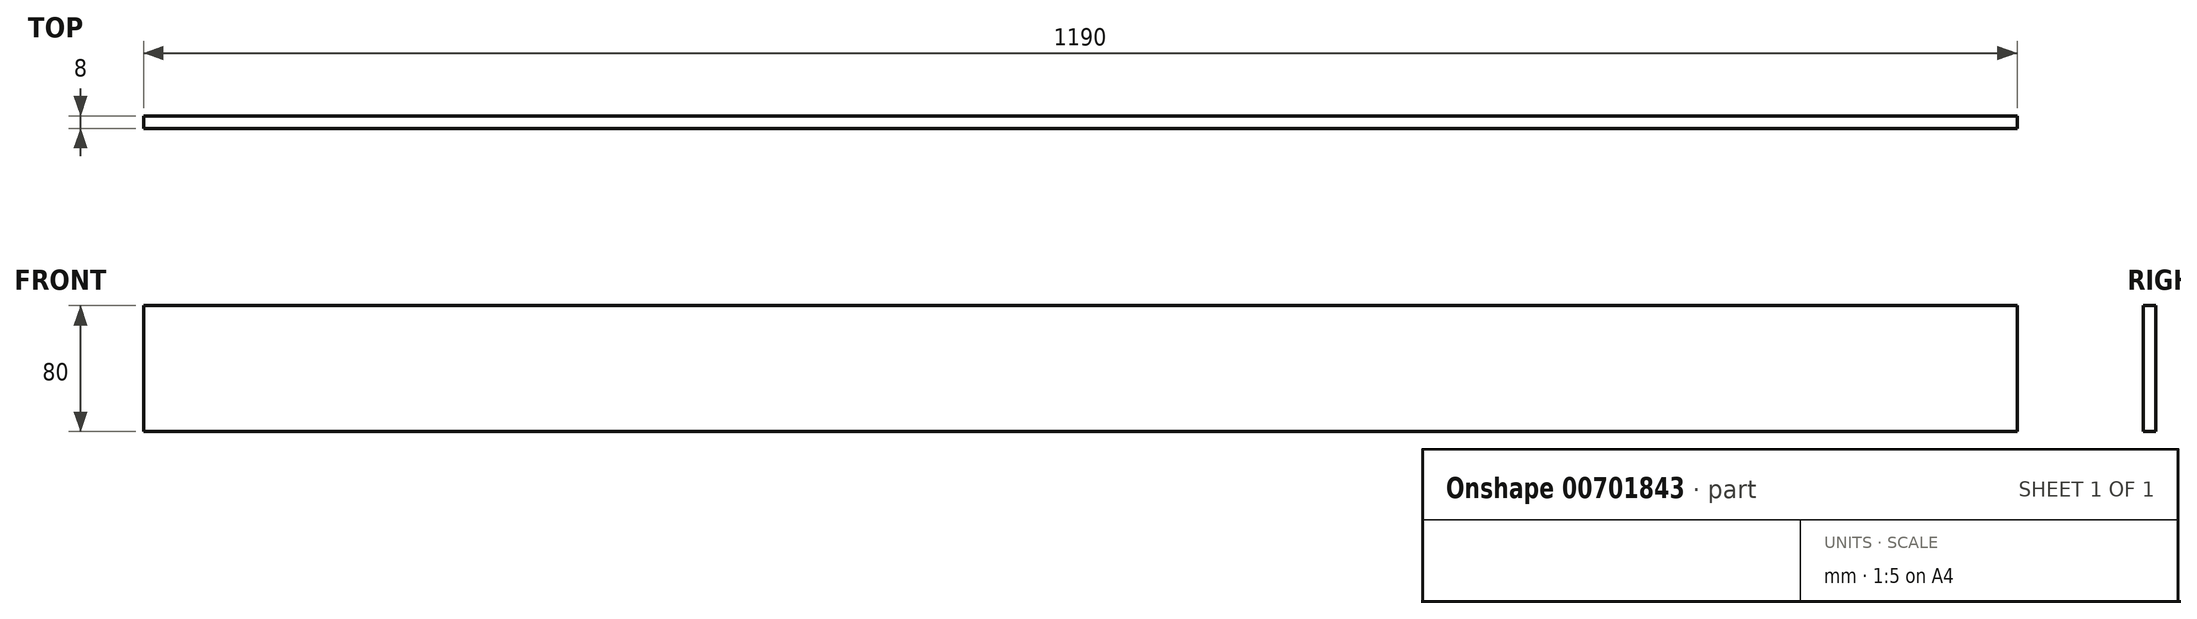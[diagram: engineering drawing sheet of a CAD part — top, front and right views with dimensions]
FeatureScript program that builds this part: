
annotation { "Feature Type Name" : "Feature", "Feature Type Description" : "" }
export const myFeature = defineFeature(function(context is Context, id is Id, definition is map)
    precondition{}
    {
        {
            var Q0;
            Q0=qCreatedBy(makeId("Front.planeOp"),FACE);
            var sketch = newSketch(context, id + "F0", { "sketchPlane" : qUnion([Q0])});
            skLineSegment(sketch, "E0.bottom", {"start": v(0, 0) * mm, "end": v(1190, 0) * mm});
            skLineSegment(sketch, "E0.top", {"start": v(0, 80) * mm, "end": v(1190, 80) * mm});
            skLineSegment(sketch, "E0.left", {"start": v(0, 0) * mm, "end": v(0, 80) * mm});
            skLineSegment(sketch, "E0.right", {"start": v(1190, 0) * mm, "end": v(1190, 80) * mm});
            skSolve(sketch);
        }
        {
            var Q0;
            Q0=makeQuery(id+"F0.imprint","IMPRINT",FACE,{"disambiguationData":[TD([[makeQuery(id+"F0.imprint","IMPRINT",EDGE,{"derivedFrom":sQuery(id+"F0.wireOp",EDGE,"E0.bottom")}),1.0]])]});
            extrude(context, id + "F1", {"entities" : qUnion([Q0]), "depth" : 8 * mm, "offsetDistance" : 25 * mm});
        }
    });
